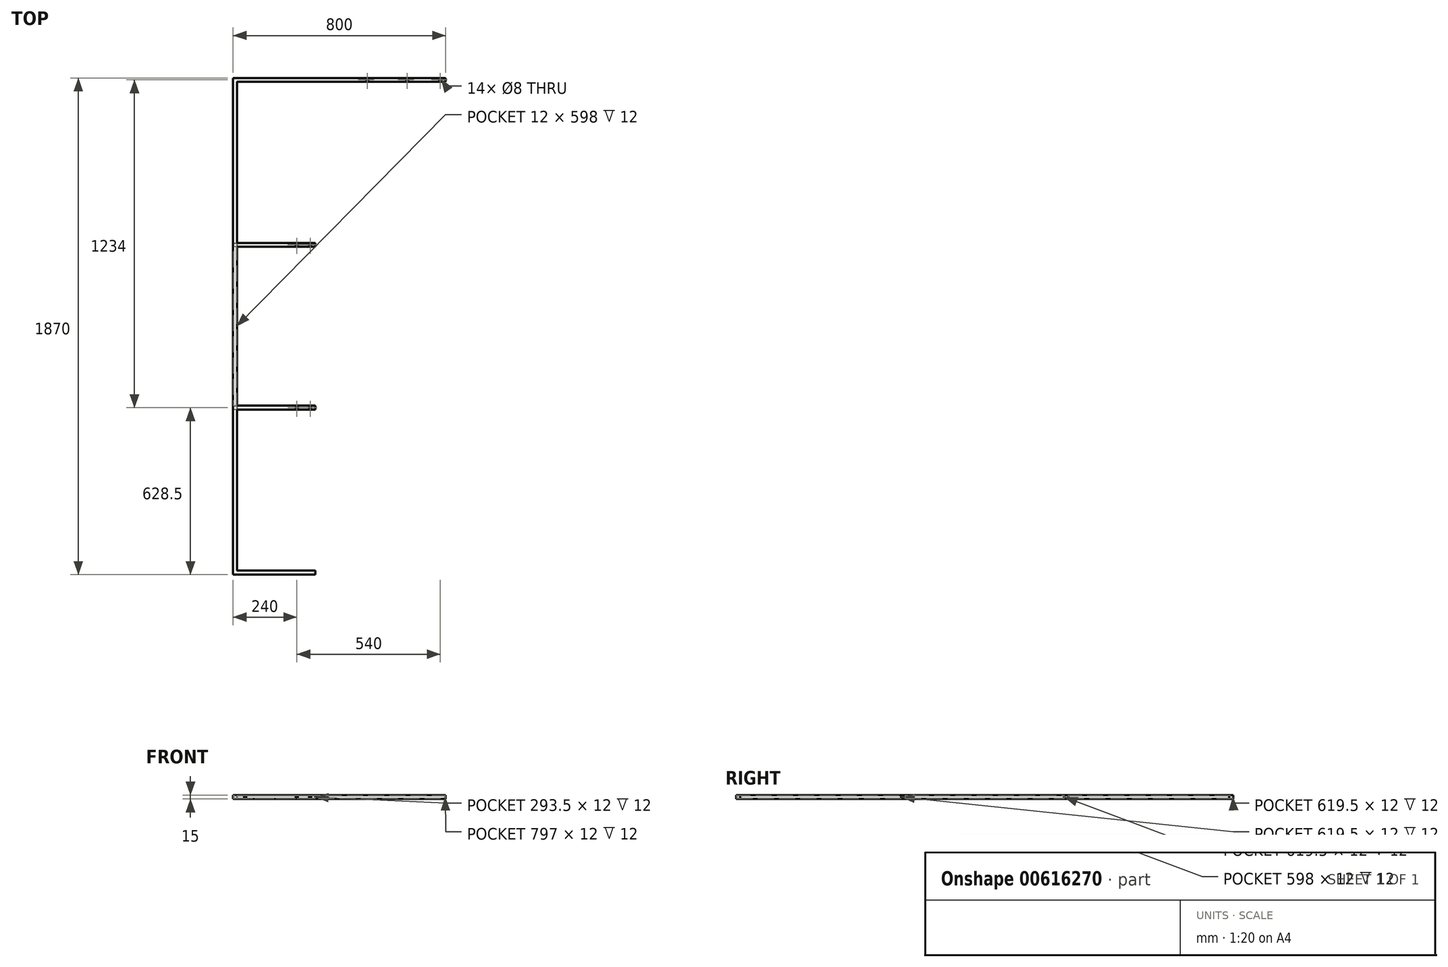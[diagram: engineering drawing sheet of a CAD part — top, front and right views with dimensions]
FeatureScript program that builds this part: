
annotation { "Feature Type Name" : "Feature", "Feature Type Description" : "" }
export const myFeature = defineFeature(function(context is Context, id is Id, definition is map)
    precondition{}
    {
        {
            var Q0;
            Q0=qCreatedBy(makeId("Top.planeOp"),FACE);
            var sketch = newSketch(context, id + "F0", { "sketchPlane" : qUnion([Q0])});
            skLineSegment(sketch, "E0", {"start": v(310, 0) * mm, "end": v(0, 0) * mm});
            skLineSegment(sketch, "E1", {"start": v(0, 0) * mm, "end": v(0, 1870) * mm});
            skLineSegment(sketch, "E2", {"start": v(0, 1870) * mm, "end": v(800, 1870) * mm});
            skLineSegment(sketch, "E3", {"start": v(0, 628.5) * mm, "end": v(310, 628.5) * mm});
            skLineSegment(sketch, "E4", {"start": v(0, 1241.5) * mm, "end": v(310, 1241.5) * mm});
            skSolve(sketch);
        }
        {
            var Q0;
            Q0=qCreatedBy(makeId("Right.planeOp"),FACE);
            var sketch = newSketch(context, id + "F1", { "sketchPlane" : qUnion([Q0])});
            skLineSegment(sketch, "E5.bottom", {"start": v(0, 0) * mm, "end": v(15, 0) * mm});
            skLineSegment(sketch, "E5.top", {"start": v(0, 15) * mm, "end": v(15, 15) * mm});
            skLineSegment(sketch, "E5.left", {"start": v(0, 0) * mm, "end": v(0, 15) * mm});
            skLineSegment(sketch, "E5.right", {"start": v(15, 0) * mm, "end": v(15, 15) * mm});
            skLineSegment(sketch, "E6.0", {"start": v(1.5, 1.5) * mm, "end": v(13.5, 1.5) * mm});
            skLineSegment(sketch, "E6.1", {"start": v(1.5, 1.5) * mm, "end": v(1.5, 13.5) * mm});
            skLineSegment(sketch, "E6.2", {"start": v(1.5, 13.5) * mm, "end": v(13.5, 13.5) * mm});
            skLineSegment(sketch, "E6.3", {"start": v(13.5, 1.5) * mm, "end": v(13.5, 13.5) * mm});
            skLineSegment(sketch, "E7.bottom", {"start": v(621, 0) * mm, "end": v(636, 0) * mm});
            skLineSegment(sketch, "E7.top", {"start": v(621, 15) * mm, "end": v(636, 15) * mm});
            skLineSegment(sketch, "E7.left", {"start": v(621, 0) * mm, "end": v(621, 15) * mm});
            skLineSegment(sketch, "E7.right", {"start": v(636, 0) * mm, "end": v(636, 15) * mm});
            skLineSegment(sketch, "E8.0", {"start": v(622.5, 13.5) * mm, "end": v(634.5, 13.5) * mm});
            skLineSegment(sketch, "E8.1", {"start": v(622.5, 1.5) * mm, "end": v(622.5, 13.5) * mm});
            skLineSegment(sketch, "E8.2", {"start": v(622.5, 1.5) * mm, "end": v(634.5, 1.5) * mm});
            skLineSegment(sketch, "E8.3", {"start": v(634.5, 1.5) * mm, "end": v(634.5, 13.5) * mm});
            skLineSegment(sketch, "E9.bottom", {"start": v(1234, 0) * mm, "end": v(1249, 0) * mm});
            skLineSegment(sketch, "E9.top", {"start": v(1234, 15) * mm, "end": v(1249, 15) * mm});
            skLineSegment(sketch, "E9.left", {"start": v(1234, 0) * mm, "end": v(1234, 15) * mm});
            skLineSegment(sketch, "E9.right", {"start": v(1249, 0) * mm, "end": v(1249, 15) * mm});
            skLineSegment(sketch, "E10.0", {"start": v(1235.5, 13.5) * mm, "end": v(1247.5, 13.5) * mm});
            skLineSegment(sketch, "E10.1", {"start": v(1235.5, 1.5) * mm, "end": v(1235.5, 13.5) * mm});
            skLineSegment(sketch, "E10.2", {"start": v(1235.5, 1.5) * mm, "end": v(1247.5, 1.5) * mm});
            skLineSegment(sketch, "E10.3", {"start": v(1247.5, 1.5) * mm, "end": v(1247.5, 13.5) * mm});
            skSolve(sketch);
        }
        {
            var Q0;
            Q0=makeQuery(id+"F1.imprint","IMPRINT",FACE,{"disambiguationData":[TD([[makeQuery(id+"F1.imprint","IMPRINT",EDGE,{"derivedFrom":sQuery(id+"F1.wireOp",EDGE,"E5.bottom")}),1.0]])]});
            var Q1;
            Q1=sQuery(id+"F0.wireOp",EDGE,"E0");
            var Q2;
            Q2=sQuery(id+"F0.wireOp",EDGE,"E1");
            var Q3;
            Q3=sQuery(id+"F0.wireOp",EDGE,"E2");
            sweep(context, id + "F2", {"profiles" : qUnion([Q0]), "path" : qUnion([Q1, Q2, Q3])});
        }
        {
            var Q0;
            Q0=makeQuery(id+"F1.imprint","IMPRINT",FACE,{"disambiguationData":[TD([[makeQuery(id+"F1.imprint","IMPRINT",EDGE,{"derivedFrom":sQuery(id+"F1.wireOp",EDGE,"E7.bottom")}),1.0]])]});
            var Q1;
            Q1=makeQuery(id+"F1.imprint","IMPRINT",FACE,{"disambiguationData":[TD([[makeQuery(id+"F1.imprint","IMPRINT",EDGE,{"derivedFrom":sQuery(id+"F1.wireOp",EDGE,"E9.bottom")}),1.0]])]});
            var Q2;
            Q2=sQuery(id+"F0.wireOp",EDGE,"E3");
            sweep(context, id + "F3", {"operationType" : NewBodyOperationType.ADD, "profiles" : qUnion([Q0, Q1]), "path" : qUnion([Q2])});
        }
        {
            var Q0;
            Q0=makeQuery(id+"F2.opSweep","CAP_FACE",FACE,{"disambiguationData":[OSD([sQuery(id+"F0.wireOp",VERTEX,"E0.start"),sQuery(id+"F1.wireOp",EDGE,"E5.bottom"),sQuery(id+"F1.wireOp",EDGE,"E5.top"),sQuery(id+"F1.wireOp",EDGE,"E5.left"),sQuery(id+"F1.wireOp",EDGE,"E5.right"),sQuery(id+"F1.wireOp",EDGE,"E6.0"),sQuery(id+"F1.wireOp",EDGE,"E6.1"),sQuery(id+"F1.wireOp",EDGE,"E6.2"),sQuery(id+"F1.wireOp",EDGE,"E6.3")])],"isStart":false});
            var sketch = newSketch(context, id + "F4", { "sketchPlane" : qUnion([Q0])});
            skLineSegment(sketch, "E11.bottom", {"start": v(0, 0) * mm, "end": v(15, 0) * mm});
            skLineSegment(sketch, "E11.top", {"start": v(0, 15) * mm, "end": v(15, 15) * mm});
            skLineSegment(sketch, "E11.left", {"start": v(0, 0) * mm, "end": v(0, 15) * mm});
            skLineSegment(sketch, "E11.right", {"start": v(15, 0) * mm, "end": v(15, 15) * mm});
            skLineSegment(sketch, "E12.bottom", {"start": v(621, 15) * mm, "end": v(636, 15) * mm});
            skLineSegment(sketch, "E12.top", {"start": v(621, 0) * mm, "end": v(636, 0) * mm});
            skLineSegment(sketch, "E12.left", {"start": v(621, 15) * mm, "end": v(621, 0) * mm});
            skLineSegment(sketch, "E12.right", {"start": v(636, 15) * mm, "end": v(636, 0) * mm});
            skLineSegment(sketch, "E13.bottom", {"start": v(1234, 15) * mm, "end": v(1249, 15) * mm});
            skLineSegment(sketch, "E13.top", {"start": v(1234, 0) * mm, "end": v(1249, 0) * mm});
            skLineSegment(sketch, "E13.left", {"start": v(1234, 15) * mm, "end": v(1234, 0) * mm});
            skLineSegment(sketch, "E13.right", {"start": v(1249, 15) * mm, "end": v(1249, 0) * mm});
            skSolve(sketch);
        }
        {
            var Q0;
            Q0 = qSketchRegion(id + "F4", true);
            extrude(context, id + "F5", {"entities" : qUnion([Q0]), "operationType" : NewBodyOperationType.ADD, "oppositeDirection" : true, "depth" : 1.5 * mm, "offsetDistance" : 25 * mm});
        }
        {
            var Q0;
            Q0=makeQuery(id+"F2.opSweep","CAP_FACE",FACE,{"disambiguationData":[OSD([sQuery(id+"F0.wireOp",VERTEX,"E2.end"),sQuery(id+"F1.wireOp",EDGE,"E5.bottom"),sQuery(id+"F1.wireOp",EDGE,"E5.top"),sQuery(id+"F1.wireOp",EDGE,"E5.left"),sQuery(id+"F1.wireOp",EDGE,"E5.right"),sQuery(id+"F1.wireOp",EDGE,"E6.0"),sQuery(id+"F1.wireOp",EDGE,"E6.1"),sQuery(id+"F1.wireOp",EDGE,"E6.2"),sQuery(id+"F1.wireOp",EDGE,"E6.3")])],"isStart":true});
            var sketch = newSketch(context, id + "F6", { "sketchPlane" : qUnion([Q0])});
            skLineSegment(sketch, "E14.bottom", {"start": v(1870, 0) * mm, "end": v(1855, 0) * mm});
            skLineSegment(sketch, "E14.top", {"start": v(1870, 15) * mm, "end": v(1855, 15) * mm});
            skLineSegment(sketch, "E14.left", {"start": v(1870, 0) * mm, "end": v(1870, 15) * mm});
            skLineSegment(sketch, "E14.right", {"start": v(1855, 0) * mm, "end": v(1855, 15) * mm});
            skSolve(sketch);
        }
        {
            var Q0;
            Q0 = qSketchRegion(id + "F6", true);
            extrude(context, id + "F7", {"entities" : qUnion([Q0]), "operationType" : NewBodyOperationType.ADD, "oppositeDirection" : true, "depth" : 1.5 * mm, "offsetDistance" : 25 * mm});
        }
        {
            var Q0;
            {var subQ0=sQuery(id+"F0.wireOp",EDGE,"E3");Q0=makeQuery(id+"F3.boolean.opBoolean","MERGE",FACE,{"derivedFrom":[makeQuery(id+"F2.opSweep","SWEPT_FACE",FACE,{"disambiguationData":[OSD([sQuery(id+"F0.wireOp",EDGE,"E2"),sQuery(id+"F1.wireOp",EDGE,"E5.top")])]}),makeQuery(id+"F3.opSweep","SWEPT_FACE",FACE,{"disambiguationData":[OSD([subQ0,sQuery(id+"F1.wireOp",EDGE,"E7.top")])]}),makeQuery(id+"F3.opSweep","SWEPT_FACE",FACE,{"disambiguationData":[OSD([subQ0,sQuery(id+"F1.wireOp",EDGE,"E9.top")])]})]});}
            var sketch = newSketch(context, id + "F8", { "sketchPlane" : qUnion([Q0])});
            skCircle(sketch, "E15", {"center": v(290, 628.5) * mm, "radius": 4 * mm});
            skPoint(sketch, "E15.centerSnap0", {"position": v(310, 628.5) * mm});
            skCircle(sketch, "E16", {"center": v(240, 628.5) * mm, "radius": 4 * mm});
            skCircle(sketch, "E17", {"center": v(290, 1241.5) * mm, "radius": 4 * mm});
            skPoint(sketch, "E17.centerSnap0", {"position": v(310, 1241.5) * mm});
            skCircle(sketch, "E18", {"center": v(240, 1241.5) * mm, "radius": 4 * mm});
            skCircle(sketch, "E19", {"center": v(780, 1862.5) * mm, "radius": 4 * mm});
            skPoint(sketch, "E19.centerSnap0", {"position": v(800, 1862.5) * mm});
            skCircle(sketch, "E20", {"center": v(655, 1862.5) * mm, "radius": 4 * mm});
            skCircle(sketch, "E21", {"center": v(505, 1862.5) * mm, "radius": 4 * mm});
            skSolve(sketch);
        }
        {
            var Q0;
            Q0 = qSketchRegion(id + "F8", true);
            var Q1;
            {var subQ0=sQuery(id+"F0.wireOp",EDGE,"E3");Q1=makeQuery(id+"F3.boolean.opBoolean","MERGE",FACE,{"derivedFrom":[makeQuery(id+"F2.opSweep","SWEPT_FACE",FACE,{"disambiguationData":[OSD([sQuery(id+"F0.wireOp",EDGE,"E2"),sQuery(id+"F1.wireOp",EDGE,"E5.bottom")])]}),makeQuery(id+"F3.opSweep","SWEPT_FACE",FACE,{"disambiguationData":[OSD([subQ0,sQuery(id+"F1.wireOp",EDGE,"E7.bottom")])]}),makeQuery(id+"F3.opSweep","SWEPT_FACE",FACE,{"disambiguationData":[OSD([subQ0,sQuery(id+"F1.wireOp",EDGE,"E9.bottom")])]})]});}
            extrude(context, id + "F9", {"entities" : qUnion([Q0]), "operationType" : NewBodyOperationType.REMOVE, "endBound" : BoundingType.UP_TO_SURFACE, "oppositeDirection" : true, "depth" : 25 * mm, "endBoundEntityFace" : qUnion([Q1]), "offsetDistance" : 25 * mm});
        }
        {
            var Q0;
            Q0=makeQuery(id+"F2.opSweep","SWEPT_FACE",FACE,{"disambiguationData":[OSD([sQuery(id+"F0.wireOp",EDGE,"E0"),sQuery(id+"F1.wireOp",EDGE,"E5.left")])]});
            var sketch = newSketch(context, id + "F10", { "sketchPlane" : qUnion([Q0])});
            skCircle(sketch, "E22", {"center": v(290, 7.5) * mm, "radius": 4 * mm});
            skPoint(sketch, "E22.centerSnap0", {"position": v(310, 7.5) * mm});
            skCircle(sketch, "E23", {"center": v(240, 7.5) * mm, "radius": 4 * mm});
            skCircle(sketch, "E24", {"center": v(45, 7.5) * mm, "radius": 4 * mm});
            skSolve(sketch);
        }
        {
            var Q0;
            Q0 = qSketchRegion(id + "F10", true);
            var Q1;
            Q1=makeQuery(id+"F2.opSweep","SWEPT_FACE",FACE,{"disambiguationData":[OSD([sQuery(id+"F0.wireOp",EDGE,"E0"),sQuery(id+"F1.wireOp",EDGE,"E5.right")])]});
            extrude(context, id + "F11", {"entities" : qUnion([Q0]), "operationType" : NewBodyOperationType.REMOVE, "endBound" : BoundingType.UP_TO_SURFACE, "oppositeDirection" : true, "depth" : 25 * mm, "endBoundEntityFace" : qUnion([Q1]), "offsetDistance" : 25 * mm});
        }
    });
